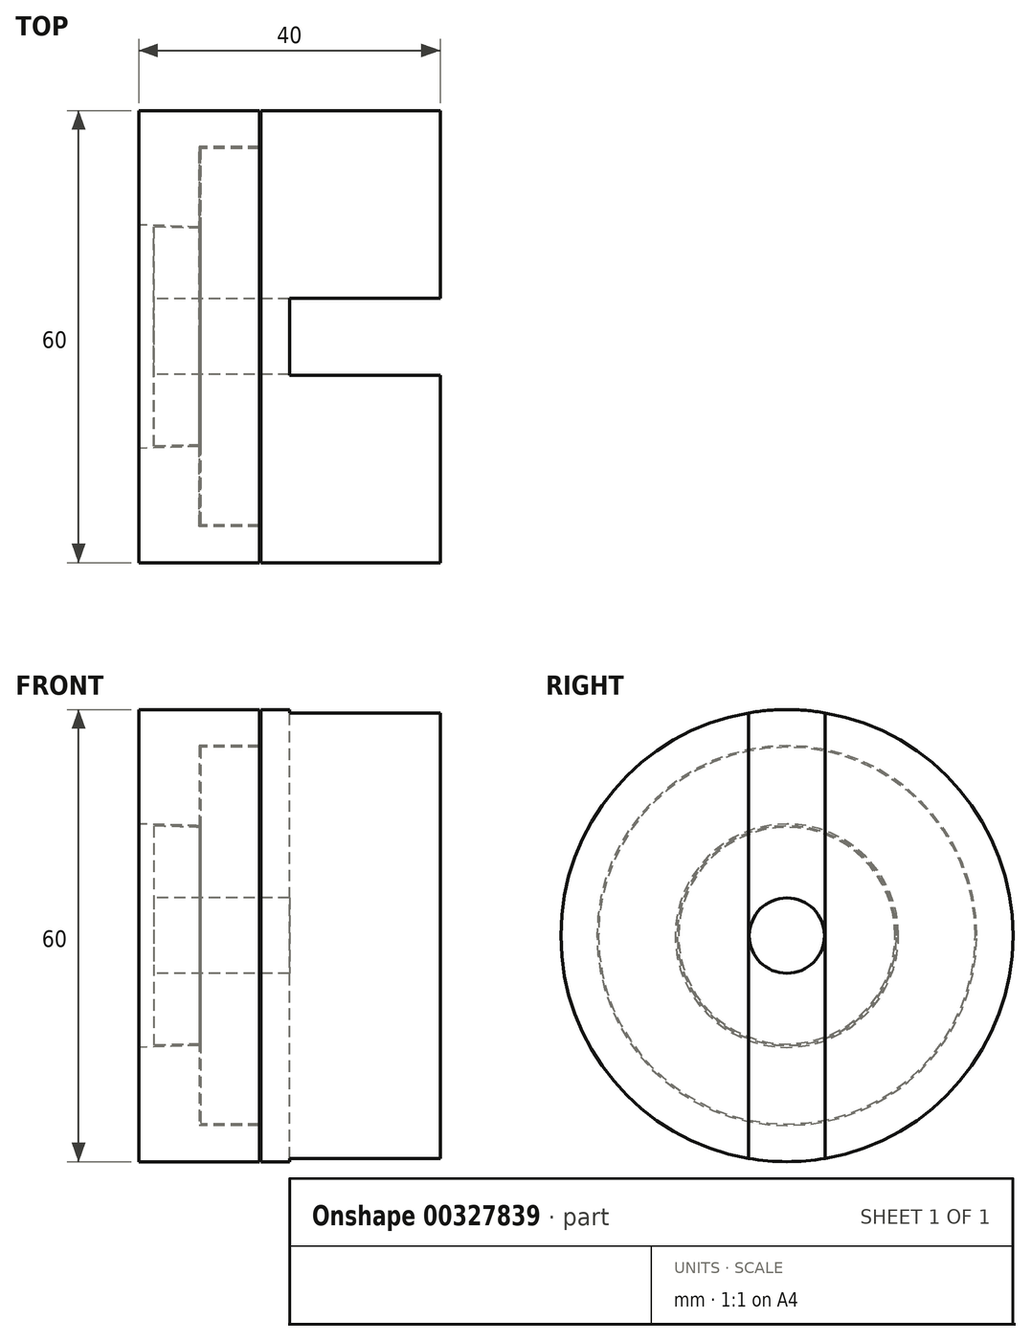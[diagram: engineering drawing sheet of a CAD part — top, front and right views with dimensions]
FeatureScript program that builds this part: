
annotation { "Feature Type Name" : "Feature", "Feature Type Description" : "" }
export const myFeature = defineFeature(function(context is Context, id is Id, definition is map)
    precondition{}
    {
        {
            var Q0;
            Q0=qCreatedBy(makeId("Top.planeOp"),FACE);
            var sketch = newSketch(context, id + "F0", { "sketchPlane" : qUnion([Q0])});
            skLineSegment(sketch, "E0", {"start": v(0, 0) * mm, "end": v(0, -30) * mm});
            skLineSegment(sketch, "E1", {"start": v(0, -30) * mm, "end": v(16, -30) * mm});
            skLineSegment(sketch, "E2", {"start": v(16, -30) * mm, "end": v(16, -25.2) * mm});
            skLineSegment(sketch, "E3", {"start": v(16, -25.2) * mm, "end": v(8, -25.2) * mm});
            skLineSegment(sketch, "E4", {"start": v(8, -25.2) * mm, "end": v(8, -14.58) * mm});
            skLineSegment(sketch, "E5", {"start": v(8.2, -25) * mm, "end": v(16.2, -25) * mm});
            skLineSegment(sketch, "E6", {"start": v(16.2, -25) * mm, "end": v(16.2, -30) * mm});
            skLineSegment(sketch, "E7", {"start": v(16.2, -30) * mm, "end": v(40, -30) * mm});
            skLineSegment(sketch, "E8", {"start": v(40, -30) * mm, "end": v(40, -5) * mm});
            skLineSegment(sketch, "E9", {"start": v(40, -5) * mm, "end": v(2, -5) * mm});
            skLineSegment(sketch, "E10", {"start": v(8, -14.58) * mm, "end": v(0, -14.82) * mm});
            skLineSegment(sketch, "E11", {"start": v(8.2, -25) * mm, "end": v(8.2, -14.37) * mm});
            skLineSegment(sketch, "E12", {"start": v(8.2, -14.37) * mm, "end": v(2, -14.56) * mm});
            skLineSegment(sketch, "E13", {"start": v(2, -14.56) * mm, "end": v(2, -5) * mm});
            skLineSegment(sketch, "E14", {"start": v(0, 0) * mm, "end": v(52.88, 0) * mm, "construction": true});
            skSolve(sketch);
        }
        {
            var Q0;
            Q0 = qSketchRegion(id + "F0", true);
            var Q1;
            Q1=sQuery(id+"F0.wireOp",EDGE,"E14");
            revolve(context, id + "F1", {"entities" : qUnion([Q0]), "axis" : qUnion([Q1]), "revolveType" : RevolveType.FULL});
        }
        {
            var Q0;
            Q0=qCreatedBy(makeId("Top.planeOp"),FACE);
            var sketch = newSketch(context, id + "F2", { "sketchPlane" : qUnion([Q0])});
            skLineSegment(sketch, "E15.bottom", {"start": v(20, 5.1) * mm, "end": v(60, 5.1) * mm});
            skLineSegment(sketch, "E15.top", {"start": v(20, -5.1) * mm, "end": v(60, -5.1) * mm});
            skLineSegment(sketch, "E15.left", {"start": v(20, 5.1) * mm, "end": v(20, -5.1) * mm});
            skLineSegment(sketch, "E15.right", {"start": v(60, 5.1) * mm, "end": v(60, -5.1) * mm});
            skPoint(sketch, "E15.middle", {"position": v(40, 0) * mm});
            skSolve(sketch);
        }
        {
            var Q0;
            Q0=makeQuery(id+"F2.imprint","IMPRINT",FACE,{"disambiguationData":[TD([[makeQuery(id+"F2.imprint","IMPRINT",EDGE,{"derivedFrom":sQuery(id+"F2.wireOp",EDGE,"E15.bottom")}),-1.0]])]});
            extrude(context, id + "F3", {"entities" : qUnion([Q0]), "operationType" : NewBodyOperationType.REMOVE, "endBound" : BoundingType.THROUGH_ALL, "oppositeDirection" : true, "depth" : 25 * mm, "hasSecondDirection" : true, "secondDirectionBound" : SecondDirectionBoundingType.THROUGH_ALL, "secondDirectionOppositeDirection" : false, "secondDirectionDepth" : 25 * mm});
        }
    });
